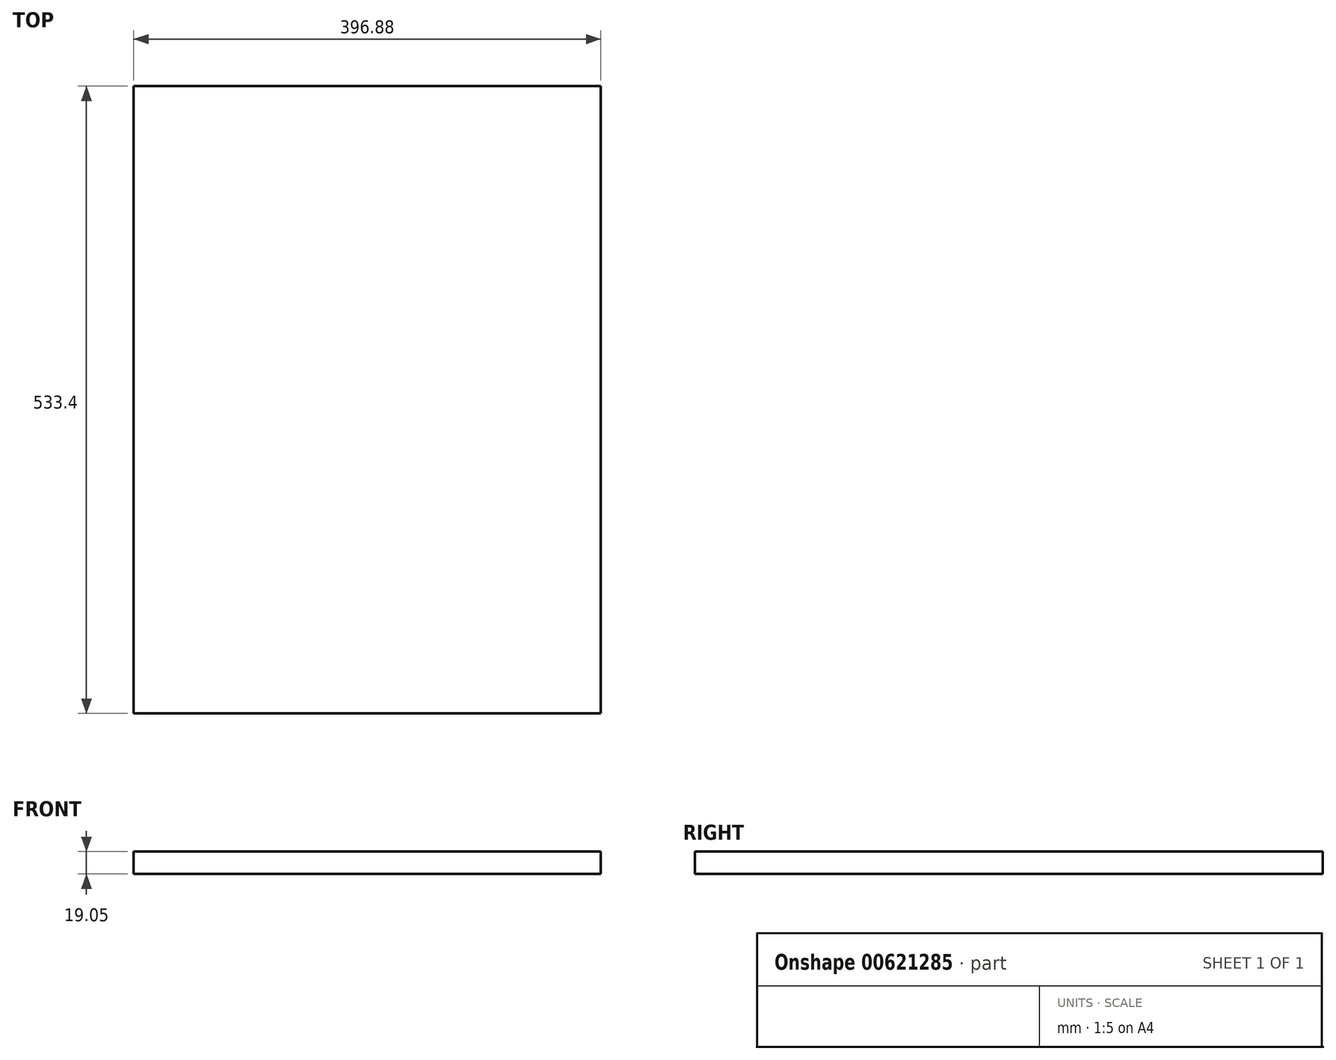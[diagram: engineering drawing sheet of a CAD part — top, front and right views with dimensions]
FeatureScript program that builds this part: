
annotation { "Feature Type Name" : "Feature", "Feature Type Description" : "" }
export const myFeature = defineFeature(function(context is Context, id is Id, definition is map)
    precondition{}
    {
        {
            var Q0;
            Q0=qCreatedBy(makeId("Top.planeOp"),FACE);
            var sketch = newSketch(context, id + "F0", { "sketchPlane" : qUnion([Q0])});
            skLineSegment(sketch, "E0.bottom", {"start": v(198.44, 266.7) * mm, "end": v(-198.44, 266.7) * mm});
            skLineSegment(sketch, "E0.top", {"start": v(198.44, -266.7) * mm, "end": v(-198.44, -266.7) * mm});
            skLineSegment(sketch, "E0.left", {"start": v(198.44, 266.7) * mm, "end": v(198.44, -266.7) * mm});
            skLineSegment(sketch, "E0.right", {"start": v(-198.44, 266.7) * mm, "end": v(-198.44, -266.7) * mm});
            skPoint(sketch, "E0.middle", {"position": v(0, 0) * mm});
            skSolve(sketch);
        }
        {
            var Q0;
            Q0=makeQuery(id+"F0.imprint","IMPRINT",FACE,{"disambiguationData":[TD([[makeQuery(id+"F0.imprint","IMPRINT",EDGE,{"derivedFrom":sQuery(id+"F0.wireOp",EDGE,"E0.bottom")}),1.0]])]});
            extrude(context, id + "F1", {"entities" : qUnion([Q0]), "depth" : 19.05 * mm, "offsetDistance" : 25.4 * mm});
        }
    });
